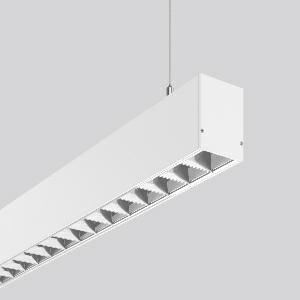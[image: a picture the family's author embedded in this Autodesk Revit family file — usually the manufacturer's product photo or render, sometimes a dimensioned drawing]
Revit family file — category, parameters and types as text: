
# Revit family: less_is_more_50_312341_002_1_fd4c
name_source: partatom
category: Lighting Fixtures
units: mm (PartAtom-declared; Revit-internal decimal feet)

## family parameters
Cut with Voids When Loaded = No
Host = Face
Light Source = No
Part Type = Normal
Room Calculation Point = No
Round Connector Dimension = Use Diameter
Shared = No

## types (1)
- LESS IS MORE 50 (1 x LED Modul 840, 4200 lm, 4000)
    Apparent Load = 35 VA
    CIE Flux Codes = 95 100 100 63 100
    Color Rendering = 80
    Color Temperature = 4000
    Default Elevation = 1800 mm
    Description = Series: LESS IS MORE 50
Linear pendant luminaire for aesthetically sophisticated lighting. Housing: extruded aluminium profile, powder-coated. End cap aluminium powder-coated. Canopy made of aluminium, powder-coated. Alea optical system: Reflector structure (ABS, Aluminium-coated, highly polished) with integrated diffuser made of non-yellowing plastic (PMMA) opal for glare-free light at the workstation (screen-compliant according to EN 12464-1). Direct 65%, indirect 35% light emission. Suitable for pendant. 2-point steel cable suspension freely positionable and infinitely height-adjustable. Special lengths available on request. LED unit with integrated converter interchangeable and removable. Suitable for through-wiring. With sensors or as a safety luminaire on request. 
Colour: traffic white, matt (RAL 9016)
Length: 847 mm
Width: 57 mm
Height: 75 mm
Suspension length: 2000 mm
Lamp: LED
Socket: without socket
Colour temperature: 4000K
Colour rendering index (CRI): 80
Light source: LED
Socket lamp2: Without base
Colour temperature: 4000K
System power: 35 W
Rated luminous flux: 4200 lm
Luminous efficiency: 120 lm/W
Control gear: Regulated power supply
Control gear: Regulated power supply
Protection class: I
Type of protection: IP 20
    Height = 75 mm
    Lamp = 1 x LED Modul 840
    Lamp Light Flux = 4200 lm
    Lamp count = 1
    Length = 847 mm
    Lifetime = 50000 h
    Luminous efficacy = 120 lm/W
    Manufacturer = RZB
    ModVariant = No
    Model = 312341.002.1
    Mounting Place = Ceiling
    Mounting Type = Pendant
    Number of Poles = 1
    OnlyDefault = Yes
    Power Factor = 1
    Product Name = LESS IS MORE 50
    Product group = Pendant LED linear luminaires
    ProductGroupID = 907
    Protection Class = Protection class I
    Protection Degree = IP 20
    RLX_Detail_Level = 1
    RLX_Emergency_Light_Flux = 0 lm
    RLX_Emergency_Type = 0
    RLX_Emergency_Type_DB = No
    RlxData = <blob elided: 37413 chars, md5=9987a9de>
    Socket = socket
    Standby Power = 0 W
    System Light Flux = 4200 lm
    System Power = 35 W
    Type Comments = Product without accessories
    Type Image = 312342.002.jpg
    URL = http://relux.com
    VarID = ---
    Voltage = 230 V
    Voltage Range = 220-240 V
    Weight = 0.00 kg
    Width = 57 mm

## geometry (parser evidence)
native form markers: Blend x4, Sweep x14
no freeform markers — native parametric forms only
